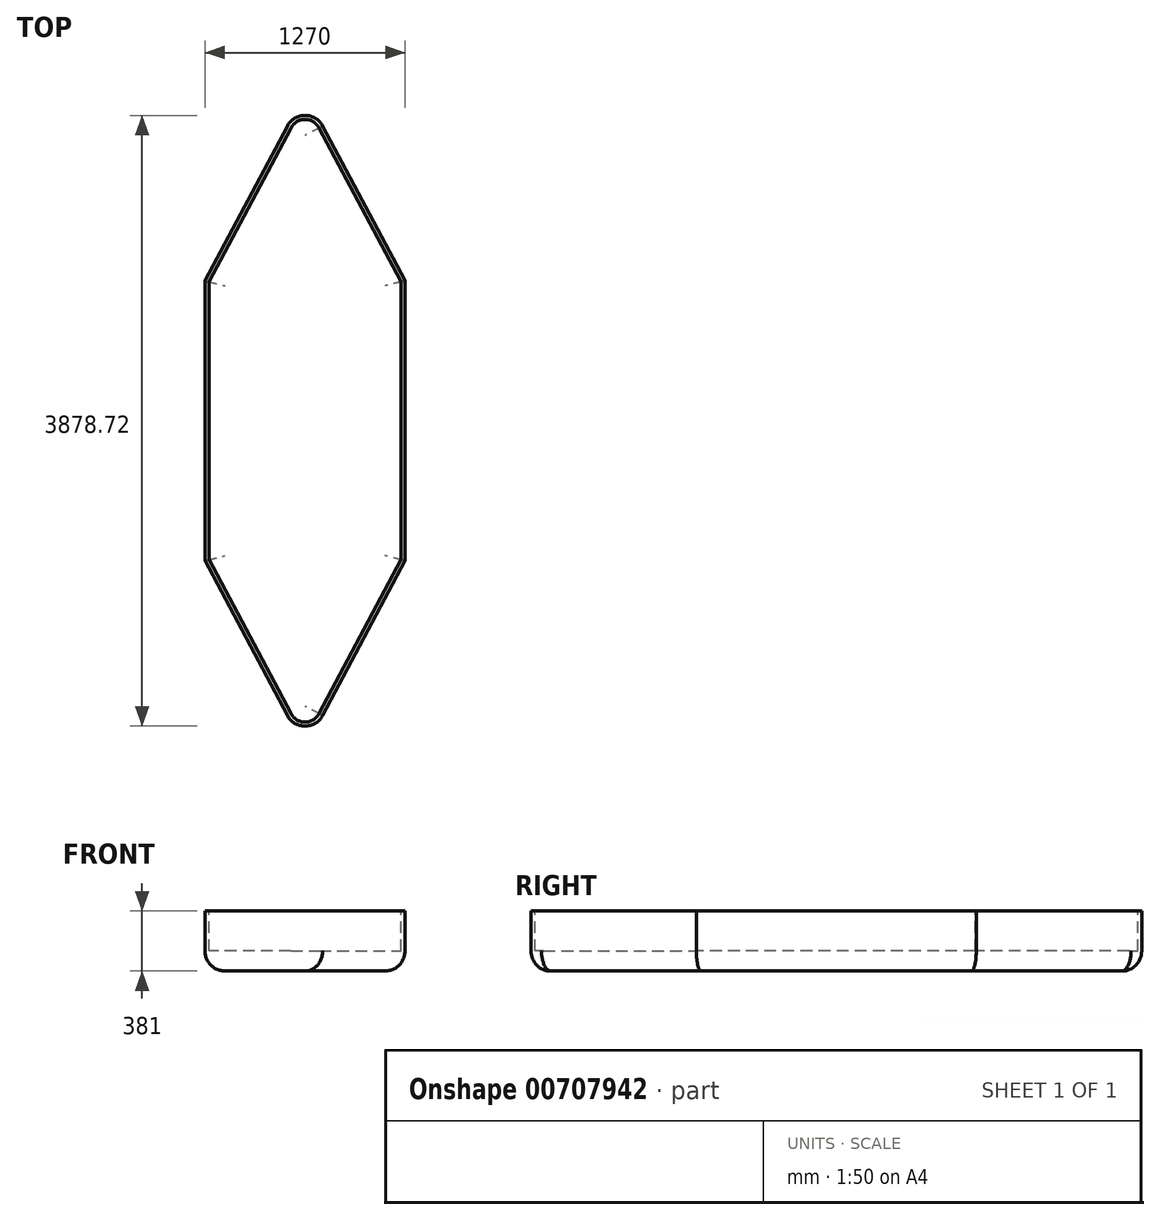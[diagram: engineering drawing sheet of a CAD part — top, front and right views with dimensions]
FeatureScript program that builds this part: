
annotation { "Feature Type Name" : "Feature", "Feature Type Description" : "" }
export const myFeature = defineFeature(function(context is Context, id is Id, definition is map)
    precondition{}
    {
        {
            var Q0;
            Q0=qCreatedBy(makeId("Top.planeOp"),FACE);
            var sketch = newSketch(context, id + "F0", { "sketchPlane" : qUnion([Q0])});
            skLineSegment(sketch, "E0", {"start": v(0, 0) * mm, "end": v(0, 2082.8) * mm});
            skLineSegment(sketch, "E1", {"start": v(0, 2082.8) * mm, "end": v(635, 889) * mm});
            skLineSegment(sketch, "E2", {"start": v(635, 889) * mm, "end": v(635, 0) * mm});
            skLineSegment(sketch, "E3.MirrorCS", {"start": v(0, 2082.8) * mm, "end": v(-635, 889) * mm});
            skLineSegment(sketch, "E4.MirrorCS", {"start": v(-635, 889) * mm, "end": v(-635, 0) * mm});
            skLineSegment(sketch, "E5", {"start": v(-635, 0) * mm, "end": v(635, 0) * mm});
            skLineSegment(sketch, "E6.MirrorCS", {"start": v(635, -889) * mm, "end": v(635, 0) * mm});
            skLineSegment(sketch, "E7.MirrorCS", {"start": v(-635, -889) * mm, "end": v(-635, 0) * mm});
            skLineSegment(sketch, "E8.MirrorCS", {"start": v(0, -2082.8) * mm, "end": v(-635, -889) * mm});
            skLineSegment(sketch, "E9.MirrorCS", {"start": v(0, -2082.8) * mm, "end": v(635, -889) * mm});
            skSolve(sketch);
        }
        {
            var Q0;
            Q0 = qSketchRegion(id + "F0", true);
            extrude(context, id + "F1", {"entities" : qUnion([Q0]), "depth" : 381 * mm, "offsetDistance" : 25.4 * mm});
        }
        {
            var Q0;
            Q0=makeQuery(id+"F1.opExtrude","CAP_EDGE",EDGE,{"disambiguationData":[OSD([sQuery(id+"F0.wireOp",EDGE,"E2"),sQuery(id+"F0.wireOp",EDGE,"E6.MirrorCS")])],"isStart":true});
            var Q1;
            Q1=makeQuery(id+"F1.opExtrude","CAP_EDGE",EDGE,{"disambiguationData":[OSD([sQuery(id+"F0.wireOp",EDGE,"E9.MirrorCS")])],"isStart":true});
            var Q2;
            Q2=makeQuery(id+"F1.opExtrude","CAP_EDGE",EDGE,{"disambiguationData":[OSD([sQuery(id+"F0.wireOp",EDGE,"E1")])],"isStart":true});
            fillet(context, id + "F2", {"entities" : qUnion([Q0, Q1, Q2]), "radius" : 127 * mm, "tangentPropagation" : true, "allowEdgeOverflow" : false});
        }
        {
            var Q0;
            Q0=makeQuery(id+"F1.opExtrude","CAP_EDGE",EDGE,{"disambiguationData":[OSD([sQuery(id+"F0.wireOp",EDGE,"E3.MirrorCS")])],"isStart":true});
            var Q1;
            Q1=makeQuery(id+"F1.opExtrude","CAP_EDGE",EDGE,{"disambiguationData":[OSD([sQuery(id+"F0.wireOp",EDGE,"E4.MirrorCS"),sQuery(id+"F0.wireOp",EDGE,"E7.MirrorCS")])],"isStart":true});
            var Q2;
            Q2=makeQuery(id+"F1.opExtrude","CAP_EDGE",EDGE,{"disambiguationData":[OSD([sQuery(id+"F0.wireOp",EDGE,"E8.MirrorCS")])],"isStart":true});
            fillet(context, id + "F3", {"entities" : qUnion([Q0, Q1, Q2]), "radius" : 127 * mm, "tangentPropagation" : true, "allowEdgeOverflow" : false});
        }
        {
            var Q0;
            Q0=makeQuery(id+"F1.opExtrude","CAP_FACE",FACE,{"disambiguationData":[OSD([sQuery(id+"F0.wireOp",EDGE,"E1"),sQuery(id+"F0.wireOp",EDGE,"E2"),sQuery(id+"F0.wireOp",EDGE,"E3.MirrorCS"),sQuery(id+"F0.wireOp",EDGE,"E4.MirrorCS"),sQuery(id+"F0.wireOp",EDGE,"E6.MirrorCS"),sQuery(id+"F0.wireOp",EDGE,"E7.MirrorCS"),sQuery(id+"F0.wireOp",EDGE,"E8.MirrorCS"),sQuery(id+"F0.wireOp",EDGE,"E9.MirrorCS")])],"isStart":false});
            var sketch = newSketch(context, id + "F4", { "sketchPlane" : qUnion([Q0])});
            skLineSegment(sketch, "E10.0", {"start": v(-89.7, -1860.08) * mm, "end": v(-609.6, -882.66) * mm});
            skLineSegment(sketch, "E10.1", {"start": v(-609.6, 889) * mm, "end": v(-609.6, -882.66) * mm});
            skArc(sketch, "E11.0", {"start": v(-89.7, -1860.08) * mm, "mid": v(0, -1913.96) * mm, "end": v(89.7, -1860.08) * mm});
            skLineSegment(sketch, "E12.0", {"start": v(89.7, 1860.08) * mm, "end": v(612.58, 877.07) * mm});
            skLineSegment(sketch, "E13.0", {"start": v(-609.6, 882.66) * mm, "end": v(-609.6, -882.66) * mm});
            skLineSegment(sketch, "E13.1", {"start": v(-89.7, 1860.08) * mm, "end": v(-609.6, 882.66) * mm});
            skLineSegment(sketch, "E13.2", {"start": v(-609.6, -882.66) * mm, "end": v(-89.7, -1860.08) * mm});
            skArc(sketch, "E13.3", {"start": v(89.7, 1860.08) * mm, "mid": v(0, 1913.96) * mm, "end": v(-89.7, 1860.08) * mm});
            skLineSegment(sketch, "E13.5", {"start": v(89.7, -1860.08) * mm, "end": v(609.6, -882.66) * mm});
            skLineSegment(sketch, "E13.6", {"start": v(609.6, -882.66) * mm, "end": v(609.6, 882.66) * mm});
            skLineSegment(sketch, "E13.7", {"start": v(609.6, 882.66) * mm, "end": v(89.7, 1860.08) * mm});
            skSolve(sketch);
        }
        {
            var Q0;
            Q0 = qSketchRegion(id + "F4", true);
            extrude(context, id + "F5", {"entities" : qUnion([Q0]), "operationType" : NewBodyOperationType.REMOVE, "oppositeDirection" : true, "depth" : 254 * mm, "offsetDistance" : 25.4 * mm});
        }
    });
